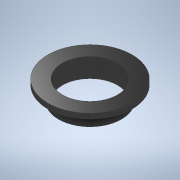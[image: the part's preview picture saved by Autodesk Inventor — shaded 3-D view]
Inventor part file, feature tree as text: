
AUTODESK INVENTOR PART (.ipt)
format: ipt  version: 2020 (Build 240168000, 168)  size: 123,904 bytes
history: native  units: in
note: dims shown in document units (in); Inventor stores cm internally (conversion verified against a paired STEP export)
features: sketch x3, extrude x2, revolve x1
ambient origin geometry x8: Origin, YZ Plane, XZ Plane, XY Plane, X Axis, Y Axis, Z Axis, Center Point
bodies: Solid1 (feature_tree)
feature tree (6):
  revolve  "Revolution1"  [1 undecoded]
  extrude  "Extrusion1"  Depth=0.25in
  extrude  "Extrusion2"  Depth=0.25in
  sketch  "Sketch1"  dims[d2=0.75in d3=0.093in]
  sketch  "Sketch2"  dims[d4=0.167in d5=0.25in]
  sketch  "Sketch3"  dims[d6=90.0deg d7=0.9843in d8=1.0in d9=0.0in d10=1.125in d11=0.25in d12=0.0in]
note: 1 required parameter value undecoded (feature->parameter linkage not recoverable at this tier; creation-order binding heuristic only, values carry confidence <= 0.55)
